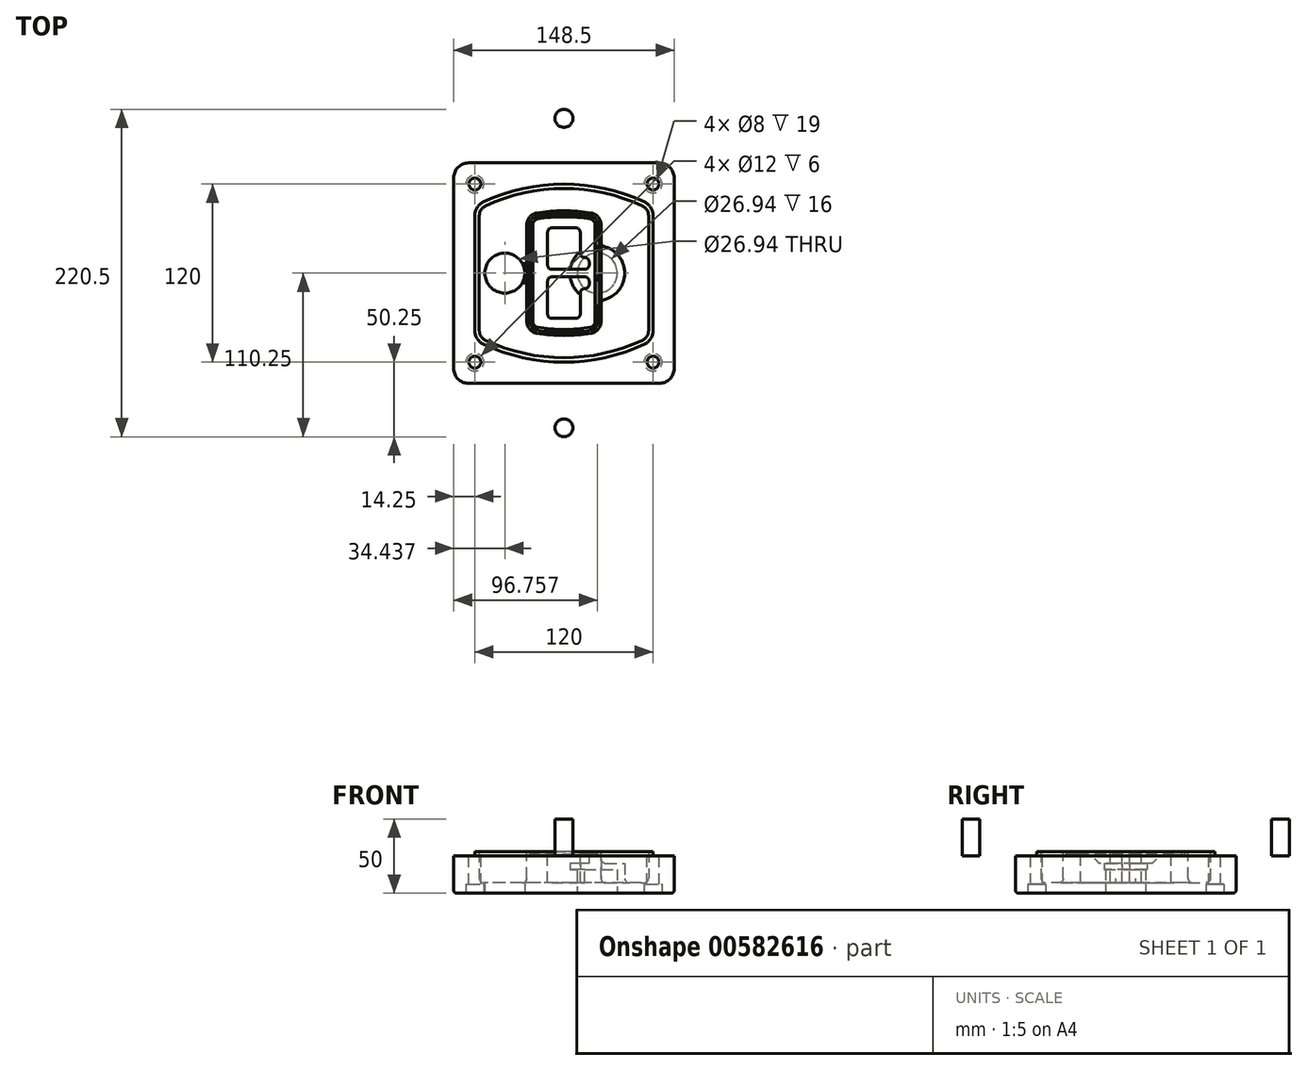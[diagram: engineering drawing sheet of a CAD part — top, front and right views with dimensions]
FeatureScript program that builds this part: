
annotation { "Feature Type Name" : "Feature", "Feature Type Description" : "" }
export const myFeature = defineFeature(function(context is Context, id is Id, definition is map)
    precondition{}
    {
        {
            var Q0;
            Q0=qCreatedBy(makeId("Top.planeOp"),FACE);
            var sketch = newSketch(context, id + "F0", { "sketchPlane" : qUnion([Q0])});
            skPoint(sketch, "E0.rect.middle", {"position": v(0, 0) * mm});
            skLineSegment(sketch, "E1.bottom", {"start": v(-64.25, -74.25) * mm, "end": v(64.25, -74.25) * mm});
            skLineSegment(sketch, "E1.top", {"start": v(-64.25, 74.25) * mm, "end": v(64.25, 74.25) * mm});
            skLineSegment(sketch, "E1.left", {"start": v(-74.25, -64.25) * mm, "end": v(-74.25, 64.25) * mm});
            skLineSegment(sketch, "E1.right", {"start": v(74.25, -64.25) * mm, "end": v(74.25, 64.25) * mm});
            skLineSegment(sketch, "E2", {"start": v(-74.25, 74.25) * mm, "end": v(74.25, -74.25) * mm, "construction": true});
            skLineSegment(sketch, "E3", {"start": v(74.25, 74.25) * mm, "end": v(-74.25, -74.25) * mm, "construction": true});
            skCircle(sketch, "E4", {"center": v(-60, 60) * mm, "radius": 4 * mm});
            skCircle(sketch, "E5", {"center": v(60, 60) * mm, "radius": 4 * mm});
            skCircle(sketch, "E6", {"center": v(60, -60) * mm, "radius": 4 * mm});
            skCircle(sketch, "E7", {"center": v(-60, -60) * mm, "radius": 4 * mm});
            skLineSegment(sketch, "E8", {"start": v(-60, 60) * mm, "end": v(60, 60) * mm, "construction": true});
            skLineSegment(sketch, "E9", {"start": v(60, 60) * mm, "end": v(60, -60) * mm, "construction": true});
            skLineSegment(sketch, "E10", {"start": v(60, -60) * mm, "end": v(-60, -60) * mm, "construction": true});
            skLineSegment(sketch, "E11", {"start": v(-60, -60) * mm, "end": v(-60, 60) * mm, "construction": true});
            skLineSegment(sketch, "E12", {"start": v(-60, 38.83) * mm, "end": v(-60, -38.83) * mm});
            skLineSegment(sketch, "E13", {"start": v(60, 38.83) * mm, "end": v(60, -38.83) * mm});
            skArc(sketch, "E14", {"start": v(54.26, 47.88) * mm, "mid": v(0, 60) * mm, "end": v(-54.26, 47.88) * mm});
            skArc(sketch, "E15", {"start": v(-54.26, -47.88) * mm, "mid": v(0, -60) * mm, "end": v(54.26, -47.88) * mm});
            skLineSegment(sketch, "E16", {"start": v(-60, 0) * mm, "end": v(60, 0) * mm, "construction": true});
            skPoint(sketch, "E17.visualSharp", {"position": v(-60, -45) * mm});
            skArc(sketch, "E17.filletArc", {"start": v(-60, -38.83) * mm, "mid": v(-58.44, -44.2) * mm, "end": v(-54.26, -47.88) * mm});
            skPoint(sketch, "E18.visualSharp", {"position": v(-60, 45) * mm});
            skArc(sketch, "E18.filletArc", {"start": v(-54.26, 47.88) * mm, "mid": v(-58.44, 44.2) * mm, "end": v(-60, 38.83) * mm});
            skPoint(sketch, "E19.visualSharp", {"position": v(60, 45) * mm});
            skArc(sketch, "E19.filletArc", {"start": v(60, 38.83) * mm, "mid": v(58.44, 44.2) * mm, "end": v(54.26, 47.88) * mm});
            skPoint(sketch, "E20.visualSharp", {"position": v(60, -45) * mm});
            skArc(sketch, "E20.filletArc", {"start": v(54.26, -47.88) * mm, "mid": v(58.44, -44.2) * mm, "end": v(60, -38.83) * mm});
            skPoint(sketch, "E21.visualSharp", {"position": v(-74.25, 74.25) * mm});
            skArc(sketch, "E21.filletArc", {"start": v(-64.25, 74.25) * mm, "mid": v(-71.32, 71.32) * mm, "end": v(-74.25, 64.25) * mm});
            skPoint(sketch, "E22.visualSharp", {"position": v(74.25, 74.25) * mm});
            skArc(sketch, "E22.filletArc", {"start": v(74.25, 64.25) * mm, "mid": v(71.32, 71.32) * mm, "end": v(64.25, 74.25) * mm});
            skPoint(sketch, "E23.visualSharp", {"position": v(74.25, -74.25) * mm});
            skArc(sketch, "E23.filletArc", {"start": v(64.25, -74.25) * mm, "mid": v(71.32, -71.32) * mm, "end": v(74.25, -64.25) * mm});
            skPoint(sketch, "E24.visualSharp", {"position": v(-74.25, -74.25) * mm});
            skArc(sketch, "E24.filletArc", {"start": v(-74.25, -64.25) * mm, "mid": v(-71.32, -71.32) * mm, "end": v(-64.25, -74.25) * mm});
            skArc(sketch, "E25.0", {"start": v(57, 38.83) * mm, "mid": v(55.9, 42.58) * mm, "end": v(52.98, 45.17) * mm});
            skLineSegment(sketch, "E25.1", {"start": v(57, 38.83) * mm, "end": v(57, -38.83) * mm});
            skArc(sketch, "E25.2", {"start": v(52.98, -45.17) * mm, "mid": v(55.9, -42.58) * mm, "end": v(57, -38.83) * mm});
            skArc(sketch, "E25.3", {"start": v(-52.98, -45.17) * mm, "mid": v(0, -57) * mm, "end": v(52.98, -45.17) * mm});
            skArc(sketch, "E25.4", {"start": v(-57, -38.83) * mm, "mid": v(-55.9, -42.58) * mm, "end": v(-52.98, -45.17) * mm});
            skArc(sketch, "E25.5", {"start": v(52.98, 45.17) * mm, "mid": v(0, 57) * mm, "end": v(-52.98, 45.17) * mm});
            skLineSegment(sketch, "E25.6", {"start": v(-57, 38.83) * mm, "end": v(-57, -38.83) * mm});
            skArc(sketch, "E25.7", {"start": v(-52.98, 45.17) * mm, "mid": v(-55.9, 42.58) * mm, "end": v(-57, 38.83) * mm});
            skArc(sketch, "E26.0", {"start": v(-55.96, 51.5) * mm, "mid": v(-61.82, 46.33) * mm, "end": v(-64, 38.83) * mm});
            skArc(sketch, "E26.1", {"start": v(55.96, 51.5) * mm, "mid": v(0, 64) * mm, "end": v(-55.96, 51.5) * mm});
            skArc(sketch, "E26.2", {"start": v(64, 38.83) * mm, "mid": v(61.82, 46.33) * mm, "end": v(55.96, 51.5) * mm});
            skLineSegment(sketch, "E26.3", {"start": v(64, 38.83) * mm, "end": v(64, -38.83) * mm});
            skArc(sketch, "E26.4", {"start": v(55.96, -51.5) * mm, "mid": v(61.82, -46.33) * mm, "end": v(64, -38.83) * mm});
            skLineSegment(sketch, "E26.5", {"start": v(-64, 38.83) * mm, "end": v(-64, -38.83) * mm});
            skArc(sketch, "E26.6", {"start": v(-55.96, -51.5) * mm, "mid": v(0, -64) * mm, "end": v(55.96, -51.5) * mm});
            skArc(sketch, "E26.7", {"start": v(-64, -38.83) * mm, "mid": v(-61.82, -46.33) * mm, "end": v(-55.96, -51.5) * mm});
            skSolve(sketch);
        }
        {
            var Q0;
            Q0=makeQuery(id+"F0.imprint","IMPRINT",FACE,{"disambiguationData":[TD([[makeQuery(id+"F0.imprint","IMPRINT",EDGE,{"derivedFrom":sQuery(id+"F0.wireOp",EDGE,"E1.bottom")}),1.0]])]});
            var Q1;
            Q1=makeQuery(id+"F0.imprint","IMPRINT",FACE,{"disambiguationData":[TD([[makeQuery(id+"F0.imprint","IMPRINT",EDGE,{"derivedFrom":sQuery(id+"F0.wireOp",EDGE,"E12")}),1.0]])]});
            var Q2;
            Q2=makeQuery(id+"F0.imprint","IMPRINT",FACE,{"disambiguationData":[TD([[makeQuery(id+"F0.imprint","IMPRINT",EDGE,{"derivedFrom":sQuery(id+"F0.wireOp",EDGE,"E25.0")}),1.0]])]});
            var Q3;
            Q3=makeQuery(id+"F0.imprint","IMPRINT",FACE,{"disambiguationData":[TD([[makeQuery(id+"F0.imprint","IMPRINT",EDGE,{"derivedFrom":sQuery(id+"F0.wireOp",EDGE,"E12")}),-1.0]])]});
            extrude(context, id + "F1", {"entities" : qUnion([Q0, Q1, Q2, Q3]), "oppositeDirection" : true, "depth" : 25 * mm});
        }
        {
            var Q0;
            Q0=makeQuery(id+"F0.imprint","IMPRINT",FACE,{"disambiguationData":[TD([[makeQuery(id+"F0.imprint","IMPRINT",EDGE,{"derivedFrom":sQuery(id+"F0.wireOp",EDGE,"E12")}),1.0]])]});
            extrude(context, id + "F2", {"entities" : qUnion([Q0]), "operationType" : NewBodyOperationType.ADD, "depth" : 3 * mm});
        }
        {
            var Q0;
            Q0=makeQuery(id+"F0.imprint","IMPRINT",FACE,{"disambiguationData":[TD([[makeQuery(id+"F0.imprint","IMPRINT",EDGE,{"derivedFrom":sQuery(id+"F0.wireOp",EDGE,"E25.0")}),1.0]])]});
            extrude(context, id + "F3", {"entities" : qUnion([Q0]), "operationType" : NewBodyOperationType.REMOVE, "oppositeDirection" : true, "depth" : 18 * mm});
        }
        {
            var Q0;
            Q0=makeQuery(id+"F2.opExtrude","CAP_FACE",FACE,{"disambiguationData":[OSD([sQuery(id+"F0.wireOp",EDGE,"E12"),sQuery(id+"F0.wireOp",EDGE,"E13"),sQuery(id+"F0.wireOp",EDGE,"E14"),sQuery(id+"F0.wireOp",EDGE,"E15"),sQuery(id+"F0.wireOp",EDGE,"E17.filletArc"),sQuery(id+"F0.wireOp",EDGE,"E18.filletArc"),sQuery(id+"F0.wireOp",EDGE,"E19.filletArc"),sQuery(id+"F0.wireOp",EDGE,"E20.filletArc"),sQuery(id+"F0.wireOp",EDGE,"E25.0"),sQuery(id+"F0.wireOp",EDGE,"E25.1"),sQuery(id+"F0.wireOp",EDGE,"E25.2"),sQuery(id+"F0.wireOp",EDGE,"E25.3"),sQuery(id+"F0.wireOp",EDGE,"E25.4"),sQuery(id+"F0.wireOp",EDGE,"E25.5"),sQuery(id+"F0.wireOp",EDGE,"E25.6"),sQuery(id+"F0.wireOp",EDGE,"E25.7")])],"isStart":false});
            var sketch = newSketch(context, id + "F4", { "sketchPlane" : qUnion([Q0])});
            skArc(sketch, "E27.0", {"start": v(-18.34, -40.45) * mm, "mid": v(0, -42) * mm, "end": v(18.34, -40.45) * mm});
            skArc(sketch, "E28.0", {"start": v(18.34, 40.45) * mm, "mid": v(0, 42) * mm, "end": v(-18.34, 40.45) * mm});
            skLineSegment(sketch, "E29", {"start": v(-25, 32.57) * mm, "end": v(-25, -32.57) * mm});
            skLineSegment(sketch, "E30", {"start": v(25, 32.57) * mm, "end": v(25, -32.57) * mm});
            skLineSegment(sketch, "E31", {"start": v(-25, 39.1) * mm, "end": v(25, 39.1) * mm, "construction": true});
            skLineSegment(sketch, "E32", {"start": v(-25, -39.1) * mm, "end": v(25, -39.1) * mm, "construction": true});
            skPoint(sketch, "E33.visualSharp", {"position": v(-25, 39.1) * mm});
            skArc(sketch, "E33.filletArc", {"start": v(-18.34, 40.45) * mm, "mid": v(-23.11, 37.73) * mm, "end": v(-25, 32.57) * mm});
            skPoint(sketch, "E34.visualSharp", {"position": v(25, 39.1) * mm});
            skArc(sketch, "E34.filletArc", {"start": v(25, 32.57) * mm, "mid": v(23.11, 37.73) * mm, "end": v(18.34, 40.45) * mm});
            skPoint(sketch, "E35.visualSharp", {"position": v(25, -39.1) * mm});
            skArc(sketch, "E35.filletArc", {"start": v(18.34, -40.45) * mm, "mid": v(23.11, -37.73) * mm, "end": v(25, -32.57) * mm});
            skPoint(sketch, "E36.visualSharp", {"position": v(-25, -39.1) * mm});
            skArc(sketch, "E36.filletArc", {"start": v(-25, -32.57) * mm, "mid": v(-23.11, -37.73) * mm, "end": v(-18.34, -40.45) * mm});
            skArc(sketch, "E37.0", {"start": v(52.98, 45.17) * mm, "mid": v(0, 57) * mm, "end": v(-52.98, 45.17) * mm});
            skArc(sketch, "E37.1", {"start": v(-52.98, 45.17) * mm, "mid": v(-55.9, 42.58) * mm, "end": v(-57, 38.83) * mm});
            skLineSegment(sketch, "E37.2", {"start": v(-57, 38.83) * mm, "end": v(-57, -38.83) * mm});
            skArc(sketch, "E37.3", {"start": v(-57, -38.83) * mm, "mid": v(-55.9, -42.58) * mm, "end": v(-52.98, -45.17) * mm});
            skArc(sketch, "E37.4", {"start": v(-52.98, -45.17) * mm, "mid": v(0, -57) * mm, "end": v(52.98, -45.17) * mm});
            skArc(sketch, "E37.5", {"start": v(52.98, -45.17) * mm, "mid": v(55.9, -42.58) * mm, "end": v(57, -38.83) * mm});
            skLineSegment(sketch, "E37.6", {"start": v(57, 38.83) * mm, "end": v(57, -38.83) * mm});
            skArc(sketch, "E37.7", {"start": v(57, 38.83) * mm, "mid": v(55.9, 42.58) * mm, "end": v(52.98, 45.17) * mm});
            skLineSegment(sketch, "E38.0", {"start": v(23, 32.57) * mm, "end": v(23, -32.57) * mm});
            skArc(sketch, "E38.1", {"start": v(18, -38.48) * mm, "mid": v(21.58, -36.44) * mm, "end": v(23, -32.57) * mm});
            skArc(sketch, "E38.2", {"start": v(-18, -38.48) * mm, "mid": v(0, -40) * mm, "end": v(18, -38.48) * mm});
            skArc(sketch, "E38.3", {"start": v(-23, -32.57) * mm, "mid": v(-21.58, -36.44) * mm, "end": v(-18, -38.48) * mm});
            skLineSegment(sketch, "E38.4", {"start": v(-23, 32.57) * mm, "end": v(-23, -32.57) * mm});
            skArc(sketch, "E38.5", {"start": v(23, 32.57) * mm, "mid": v(21.58, 36.44) * mm, "end": v(18, 38.48) * mm});
            skArc(sketch, "E38.6", {"start": v(-18, 38.48) * mm, "mid": v(-21.58, 36.44) * mm, "end": v(-23, 32.57) * mm});
            skArc(sketch, "E38.7", {"start": v(18, 38.48) * mm, "mid": v(0, 40) * mm, "end": v(-18, 38.48) * mm});
            skArc(sketch, "E39.0", {"start": v(21, 32.57) * mm, "mid": v(20.06, 35.15) * mm, "end": v(17.67, 36.5) * mm});
            skLineSegment(sketch, "E39.1", {"start": v(21, 32.57) * mm, "end": v(21, -32.57) * mm});
            skArc(sketch, "E39.2", {"start": v(17.67, -36.5) * mm, "mid": v(20.06, -35.15) * mm, "end": v(21, -32.57) * mm});
            skArc(sketch, "E39.3", {"start": v(-17.67, -36.5) * mm, "mid": v(0, -38) * mm, "end": v(17.67, -36.5) * mm});
            skArc(sketch, "E39.4", {"start": v(-21, -32.57) * mm, "mid": v(-20.06, -35.15) * mm, "end": v(-17.67, -36.5) * mm});
            skArc(sketch, "E39.5", {"start": v(17.67, 36.5) * mm, "mid": v(0, 38) * mm, "end": v(-17.67, 36.5) * mm});
            skLineSegment(sketch, "E39.6", {"start": v(-21, 32.57) * mm, "end": v(-21, -32.57) * mm});
            skArc(sketch, "E39.7", {"start": v(-17.67, 36.5) * mm, "mid": v(-20.06, 35.15) * mm, "end": v(-21, 32.57) * mm});
            skLineSegment(sketch, "E40", {"start": v(-25, 0) * mm, "end": v(25, 0) * mm, "construction": true});
            skLineSegment(sketch, "E41", {"start": v(-11, 5.5) * mm, "end": v(-11, 27.5) * mm});
            skLineSegment(sketch, "E42", {"start": v(-8, 30.5) * mm, "end": v(8, 30.5) * mm});
            skLineSegment(sketch, "E43", {"start": v(11, 27.5) * mm, "end": v(11, 13.5) * mm});
            skLineSegment(sketch, "E44", {"start": v(14, 10.5) * mm, "end": v(14, 10.5) * mm});
            skLineSegment(sketch, "E45", {"start": v(17, 7.5) * mm, "end": v(17, 5.5) * mm});
            skLineSegment(sketch, "E46", {"start": v(14, 2.5) * mm, "end": v(-8, 2.5) * mm});
            skPoint(sketch, "E47.visualSharp", {"position": v(-11, 30.5) * mm});
            skArc(sketch, "E47.filletArc", {"start": v(-8, 30.5) * mm, "mid": v(-10.12, 29.62) * mm, "end": v(-11, 27.5) * mm});
            skPoint(sketch, "E48.visualSharp", {"position": v(11, 30.5) * mm});
            skArc(sketch, "E48.filletArc", {"start": v(11, 27.5) * mm, "mid": v(10.12, 29.62) * mm, "end": v(8, 30.5) * mm});
            skPoint(sketch, "E49.visualSharp", {"position": v(11, 10.5) * mm});
            skArc(sketch, "E49.filletArc", {"start": v(11, 13.5) * mm, "mid": v(11.88, 11.38) * mm, "end": v(14, 10.5) * mm});
            skPoint(sketch, "E50.visualSharp", {"position": v(17, 10.5) * mm});
            skArc(sketch, "E50.filletArc", {"start": v(17, 7.5) * mm, "mid": v(16.12, 9.62) * mm, "end": v(14, 10.5) * mm});
            skPoint(sketch, "E51.visualSharp", {"position": v(17, 2.5) * mm});
            skArc(sketch, "E51.filletArc", {"start": v(14, 2.5) * mm, "mid": v(16.12, 3.38) * mm, "end": v(17, 5.5) * mm});
            skPoint(sketch, "E52.visualSharp", {"position": v(-11, 2.5) * mm});
            skArc(sketch, "E52.filletArc", {"start": v(-11, 5.5) * mm, "mid": v(-10.12, 3.38) * mm, "end": v(-8, 2.5) * mm});
            skLineSegment(sketch, "E53.0.MirrorCS", {"start": v(14, -2.5) * mm, "end": v(-8, -2.5) * mm});
            skArc(sketch, "E54.0.MirrorCS", {"start": v(-11, -5.5) * mm, "mid": v(-10.12, -3.38) * mm, "end": v(-8, -2.5) * mm});
            skLineSegment(sketch, "E55.0.MirrorCS", {"start": v(-11, -5.5) * mm, "end": v(-11, -27.5) * mm});
            skArc(sketch, "E56.0.MirrorCS", {"start": v(-8, -30.5) * mm, "mid": v(-10.12, -29.62) * mm, "end": v(-11, -27.5) * mm});
            skLineSegment(sketch, "E57.0.MirrorCS", {"start": v(-8, -30.5) * mm, "end": v(8, -30.5) * mm});
            skArc(sketch, "E58.0.MirrorCS", {"start": v(11, -27.5) * mm, "mid": v(10.12, -29.62) * mm, "end": v(8, -30.5) * mm});
            skLineSegment(sketch, "E59.0.MirrorCS", {"start": v(11, -27.5) * mm, "end": v(11, -13.5) * mm});
            skArc(sketch, "E60.0.MirrorCS", {"start": v(11, -13.5) * mm, "mid": v(11.88, -11.38) * mm, "end": v(14, -10.5) * mm});
            skArc(sketch, "E61.0.MirrorCS", {"start": v(17, -7.5) * mm, "mid": v(16.12, -9.62) * mm, "end": v(14, -10.5) * mm});
            skLineSegment(sketch, "E62.0.MirrorCS", {"start": v(17, -7.5) * mm, "end": v(17, -5.5) * mm});
            skArc(sketch, "E63.0.MirrorCS", {"start": v(14, -2.5) * mm, "mid": v(16.12, -3.38) * mm, "end": v(17, -5.5) * mm});
            skSolve(sketch);
        }
        {
            var Q0;
            Q0=makeQuery(id+"F4.imprint","IMPRINT",FACE,{"disambiguationData":[TD([[makeQuery(id+"F4.imprint","IMPRINT",EDGE,{"derivedFrom":sQuery(id+"F4.wireOp",EDGE,"E27.0")}),1.0]])]});
            var Q1;
            Q1=makeQuery(id+"F4.imprint","IMPRINT",FACE,{"disambiguationData":[TD([[makeQuery(id+"F4.imprint","IMPRINT",EDGE,{"derivedFrom":sQuery(id+"F4.wireOp",EDGE,"E38.0")}),-1.0]])]});
            var Q2;
            Q2=makeQuery(id+"F4.imprint","IMPRINT",FACE,{"disambiguationData":[TD([[makeQuery(id+"F4.imprint","IMPRINT",EDGE,{"derivedFrom":sQuery(id+"F4.wireOp",EDGE,"E39.0")}),1.0]])]});
            extrude(context, id + "F5", {"entities" : qUnion([Q0, Q1, Q2]), "operationType" : NewBodyOperationType.ADD, "endBound" : BoundingType.UP_TO_NEXT, "oppositeDirection" : true, "depth" : 25 * mm});
        }
        {
            var Q0;
            Q0=makeQuery(id+"F4.imprint","IMPRINT",FACE,{"disambiguationData":[TD([[makeQuery(id+"F4.imprint","IMPRINT",EDGE,{"derivedFrom":sQuery(id+"F4.wireOp",EDGE,"E38.0")}),-1.0]])]});
            extrude(context, id + "F6", {"entities" : qUnion([Q0]), "operationType" : NewBodyOperationType.REMOVE, "oppositeDirection" : true, "depth" : 2 * mm});
        }
        {
            var Q0;
            Q0=makeQuery(id+"F1.opExtrude","CAP_FACE",FACE,{"disambiguationData":[OSD([sQuery(id+"F0.wireOp",EDGE,"E1.bottom"),sQuery(id+"F0.wireOp",EDGE,"E1.top"),sQuery(id+"F0.wireOp",EDGE,"E1.left"),sQuery(id+"F0.wireOp",EDGE,"E1.right"),sQuery(id+"F0.wireOp",EDGE,"E4"),sQuery(id+"F0.wireOp",EDGE,"E5"),sQuery(id+"F0.wireOp",EDGE,"E6"),sQuery(id+"F0.wireOp",EDGE,"E7"),sQuery(id+"F0.wireOp",EDGE,"E21.filletArc"),sQuery(id+"F0.wireOp",EDGE,"E22.filletArc"),sQuery(id+"F0.wireOp",EDGE,"E23.filletArc"),sQuery(id+"F0.wireOp",EDGE,"E24.filletArc")])],"isStart":false});
            var sketch = newSketch(context, id + "F7", { "sketchPlane" : qUnion([Q0])});
            skCircle(sketch, "E64", {"center": v(22.5, 0) * mm, "radius": 13.47 * mm});
            skCircle(sketch, "E65", {"center": v(-39.81, 0) * mm, "radius": 13.47 * mm});
            skLineSegment(sketch, "E66", {"start": v(74.25, 0) * mm, "end": v(-74.25, 0) * mm});
            skCircle(sketch, "E67", {"center": v(22.5, 0) * mm, "radius": 18.47 * mm});
            skCircle(sketch, "E68", {"center": v(60, -60) * mm, "radius": 6 * mm});
            skCircle(sketch, "E69", {"center": v(-60, -60) * mm, "radius": 6 * mm});
            skCircle(sketch, "E70", {"center": v(-60, 60) * mm, "radius": 6 * mm});
            skCircle(sketch, "E71", {"center": v(60, 60) * mm, "radius": 6 * mm});
            skSolve(sketch);
        }
        {
            var Q0;
            {var subQ1=sQuery(id+"F7.wireOp",EDGE,"E66");var subQ4=sQuery(id+"F7.wireOp",EDGE,"E64");var subQ6=makeQuery(id+"F7.imprint","INTERSECT",VERTEX,{"disambiguationData":[OD(0.0)],"derivedFrom":[subQ4,subQ1]});Q0=makeQuery(id+"F7.imprint","IMPRINT",FACE,{"disambiguationData":[TD([[makeQuery(id+"F7.imprint","IMPRINT",EDGE,{"disambiguationData":[TD([[subQ6,-1.0]])],"derivedFrom":subQ4}),-1.0]])]});}
            var Q1;
            {var subQ0=sQuery(id+"F7.wireOp",EDGE,"E66");var subQ1=sQuery(id+"F7.wireOp",EDGE,"E64");var subQ3=makeQuery(id+"F7.imprint","INTERSECT",VERTEX,{"disambiguationData":[OD(0.0)],"derivedFrom":[subQ1,subQ0]});Q1=makeQuery(id+"F7.imprint","IMPRINT",FACE,{"disambiguationData":[TD([[makeQuery(id+"F7.imprint","IMPRINT",EDGE,{"disambiguationData":[TD([[subQ3,-1.0]])],"derivedFrom":subQ1}),1.0]])]});}
            var Q2;
            {var subQ0=sQuery(id+"F7.wireOp",EDGE,"E66");var subQ1=sQuery(id+"F7.wireOp",EDGE,"E64");var subQ3=makeQuery(id+"F7.imprint","INTERSECT",VERTEX,{"disambiguationData":[OD(0.0)],"derivedFrom":[subQ1,subQ0]});Q2=makeQuery(id+"F7.imprint","IMPRINT",FACE,{"disambiguationData":[TD([[makeQuery(id+"F7.imprint","IMPRINT",EDGE,{"disambiguationData":[TD([[subQ3,1.0]])],"derivedFrom":subQ1}),1.0]])]});}
            var Q3;
            {var subQ1=sQuery(id+"F7.wireOp",EDGE,"E66");var subQ4=sQuery(id+"F7.wireOp",EDGE,"E64");var subQ6=makeQuery(id+"F7.imprint","INTERSECT",VERTEX,{"disambiguationData":[OD(0.0)],"derivedFrom":[subQ4,subQ1]});Q3=makeQuery(id+"F7.imprint","IMPRINT",FACE,{"disambiguationData":[TD([[makeQuery(id+"F7.imprint","IMPRINT",EDGE,{"disambiguationData":[TD([[subQ6,1.0]])],"derivedFrom":subQ4}),-1.0]])]});}
            extrude(context, id + "F8", {"entities" : qUnion([Q0, Q1, Q2, Q3]), "operationType" : NewBodyOperationType.ADD, "oppositeDirection" : true, "depth" : 20 * mm});
        }
        {
            var Q0;
            {var subQ0=sQuery(id+"F7.wireOp",EDGE,"E66");var subQ1=sQuery(id+"F7.wireOp",EDGE,"E64");var subQ3=makeQuery(id+"F7.imprint","INTERSECT",VERTEX,{"disambiguationData":[OD(0.0)],"derivedFrom":[subQ1,subQ0]});Q0=makeQuery(id+"F7.imprint","IMPRINT",FACE,{"disambiguationData":[TD([[makeQuery(id+"F7.imprint","IMPRINT",EDGE,{"disambiguationData":[TD([[subQ3,-1.0]])],"derivedFrom":subQ1}),1.0]])]});}
            var Q1;
            {var subQ0=sQuery(id+"F7.wireOp",EDGE,"E66");var subQ1=sQuery(id+"F7.wireOp",EDGE,"E64");var subQ3=makeQuery(id+"F7.imprint","INTERSECT",VERTEX,{"disambiguationData":[OD(0.0)],"derivedFrom":[subQ1,subQ0]});Q1=makeQuery(id+"F7.imprint","IMPRINT",FACE,{"disambiguationData":[TD([[makeQuery(id+"F7.imprint","IMPRINT",EDGE,{"disambiguationData":[TD([[subQ3,1.0]])],"derivedFrom":subQ1}),1.0]])]});}
            extrude(context, id + "F9", {"entities" : qUnion([Q0, Q1]), "operationType" : NewBodyOperationType.REMOVE, "oppositeDirection" : true, "depth" : 16 * mm});
        }
        {
            var Q0;
            {var subQ0=sQuery(id+"F7.wireOp",EDGE,"E66");var subQ1=sQuery(id+"F7.wireOp",EDGE,"E65");var subQ3=makeQuery(id+"F7.imprint","INTERSECT",VERTEX,{"disambiguationData":[OD(0.0)],"derivedFrom":[subQ1,subQ0]});Q0=makeQuery(id+"F7.imprint","IMPRINT",FACE,{"disambiguationData":[TD([[makeQuery(id+"F7.imprint","IMPRINT",EDGE,{"disambiguationData":[TD([[subQ3,-1.0]])],"derivedFrom":subQ1}),1.0]])]});}
            var Q1;
            {var subQ0=sQuery(id+"F7.wireOp",EDGE,"E66");var subQ1=sQuery(id+"F7.wireOp",EDGE,"E65");var subQ3=makeQuery(id+"F7.imprint","INTERSECT",VERTEX,{"disambiguationData":[OD(0.0)],"derivedFrom":[subQ1,subQ0]});Q1=makeQuery(id+"F7.imprint","IMPRINT",FACE,{"disambiguationData":[TD([[makeQuery(id+"F7.imprint","IMPRINT",EDGE,{"disambiguationData":[TD([[subQ3,1.0]])],"derivedFrom":subQ1}),1.0]])]});}
            extrude(context, id + "F10", {"entities" : qUnion([Q0, Q1]), "operationType" : NewBodyOperationType.REMOVE, "oppositeDirection" : true, "depth" : 25 * mm});
        }
        {
            var Q0;
            Q0=makeQuery(id+"F7.imprint","IMPRINT",FACE,{"disambiguationData":[TD([[makeQuery(id+"F7.imprint","IMPRINT",EDGE,{"derivedFrom":sQuery(id+"F7.wireOp",EDGE,"E68")}),1.0]])]});
            var Q1;
            Q1=makeQuery(id+"F7.imprint","IMPRINT",FACE,{"disambiguationData":[TD([[makeQuery(id+"F7.imprint","IMPRINT",EDGE,{"derivedFrom":makeQuery(id+"F1.opExtrude","CAP_EDGE",EDGE,{"disambiguationData":[OSD([sQuery(id+"F0.wireOp",EDGE,"E5")])],"isStart":false})}),-1.0]])]});
            var Q2;
            Q2=makeQuery(id+"F7.imprint","IMPRINT",FACE,{"disambiguationData":[TD([[makeQuery(id+"F7.imprint","IMPRINT",EDGE,{"derivedFrom":sQuery(id+"F7.wireOp",EDGE,"E69")}),1.0]])]});
            var Q3;
            Q3=makeQuery(id+"F7.imprint","IMPRINT",FACE,{"disambiguationData":[TD([[makeQuery(id+"F7.imprint","IMPRINT",EDGE,{"derivedFrom":makeQuery(id+"F1.opExtrude","CAP_EDGE",EDGE,{"disambiguationData":[OSD([sQuery(id+"F0.wireOp",EDGE,"E4")])],"isStart":false})}),-1.0]])]});
            var Q4;
            Q4=makeQuery(id+"F7.imprint","IMPRINT",FACE,{"disambiguationData":[TD([[makeQuery(id+"F7.imprint","IMPRINT",EDGE,{"derivedFrom":sQuery(id+"F7.wireOp",EDGE,"E70")}),1.0]])]});
            var Q5;
            Q5=makeQuery(id+"F7.imprint","IMPRINT",FACE,{"disambiguationData":[TD([[makeQuery(id+"F7.imprint","IMPRINT",EDGE,{"derivedFrom":makeQuery(id+"F1.opExtrude","CAP_EDGE",EDGE,{"disambiguationData":[OSD([sQuery(id+"F0.wireOp",EDGE,"E7")])],"isStart":false})}),-1.0]])]});
            var Q6;
            Q6=makeQuery(id+"F7.imprint","IMPRINT",FACE,{"disambiguationData":[TD([[makeQuery(id+"F7.imprint","IMPRINT",EDGE,{"derivedFrom":sQuery(id+"F7.wireOp",EDGE,"E71")}),1.0]])]});
            var Q7;
            Q7=makeQuery(id+"F7.imprint","IMPRINT",FACE,{"disambiguationData":[TD([[makeQuery(id+"F7.imprint","IMPRINT",EDGE,{"derivedFrom":makeQuery(id+"F1.opExtrude","CAP_EDGE",EDGE,{"disambiguationData":[OSD([sQuery(id+"F0.wireOp",EDGE,"E6")])],"isStart":false})}),-1.0]])]});
            extrude(context, id + "F11", {"entities" : qUnion([Q0, Q1, Q2, Q3, Q4, Q5, Q6, Q7]), "operationType" : NewBodyOperationType.REMOVE, "oppositeDirection" : true, "depth" : 6 * mm});
        }
        {
            var Q0;
            Q0=makeQuery(id+"F9.boolean.opBoolean","COPY",FACE,{"derivedFrom":makeQuery(id+"F9.opExtrude","CAP_FACE",FACE,{"disambiguationData":[OSD([sQuery(id+"F7.wireOp",EDGE,"E64")])],"isStart":false})});
            var sketch = newSketch(context, id + "F12", { "sketchPlane" : qUnion([Q0])});
            skArc(sketch, "E72.0", {"start": v(11, 14.45) * mm, "mid": v(6.45, 9.13) * mm, "end": v(4.2, 2.5) * mm});
            skArc(sketch, "E72.1", {"start": v(4.2, -2.5) * mm, "mid": v(6.45, -9.13) * mm, "end": v(11, -14.45) * mm});
            skLineSegment(sketch, "E73", {"start": v(4.2, -2.5) * mm, "end": v(14, -2.5) * mm});
            skLineSegment(sketch, "E74.0", {"start": v(14, 2.5) * mm, "end": v(4.2, 2.5) * mm});
            skArc(sketch, "E74.1", {"start": v(14, 2.5) * mm, "mid": v(16.12, 3.38) * mm, "end": v(17, 5.5) * mm});
            skLineSegment(sketch, "E74.2", {"start": v(17, 7.5) * mm, "end": v(17, 5.5) * mm});
            skArc(sketch, "E74.3", {"start": v(17, 7.5) * mm, "mid": v(16.12, 9.62) * mm, "end": v(14, 10.5) * mm});
            skArc(sketch, "E74.4", {"start": v(11, 13.5) * mm, "mid": v(11.88, 11.38) * mm, "end": v(14, 10.5) * mm});
            skLineSegment(sketch, "E74.5", {"start": v(11, 14.45) * mm, "end": v(11, 13.5) * mm});
            skLineSegment(sketch, "E74.7", {"start": v(14, -2.5) * mm, "end": v(4.2, -2.5) * mm});
            skArc(sketch, "E74.8", {"start": v(14, -2.5) * mm, "mid": v(16.12, -3.38) * mm, "end": v(17, -5.5) * mm});
            skLineSegment(sketch, "E74.9", {"start": v(17, -7.5) * mm, "end": v(17, -5.5) * mm});
            skArc(sketch, "E74.10", {"start": v(17, -7.5) * mm, "mid": v(16.12, -9.62) * mm, "end": v(14, -10.5) * mm});
            skArc(sketch, "E74.11", {"start": v(11, -13.5) * mm, "mid": v(11.88, -11.38) * mm, "end": v(14, -10.5) * mm});
            skLineSegment(sketch, "E74.12", {"start": v(11, -14.45) * mm, "end": v(11, -13.5) * mm});
            skPoint(sketch, "E75.orphan", {"position": v(11, -27.5) * mm});
            skPoint(sketch, "E76.orphan", {"position": v(-8, -2.5) * mm});
            skPoint(sketch, "E77.orphan", {"position": v(-8, 2.5) * mm});
            skPoint(sketch, "E78.orphan", {"position": v(11, 27.5) * mm});
            skSolve(sketch);
        }
        {
            var Q0;
            {var subQ7=sQuery(id+"F12.wireOp",EDGE,"E72.0");var subQ14=sQuery(id+"F12.wireOp",EDGE,"E72.1");var subQ16=sQuery(id+"F12.wireOp",EDGE,"E74.1");var subQ18=sQuery(id+"F12.wireOp",EDGE,"E74.8");Q0=qUnion([makeQuery(id+"F12.imprint","IMPRINT",FACE,{"disambiguationData":[TD([[makeQuery(id+"F12.imprint","IMPRINT",EDGE,{"derivedFrom":subQ7}),1.0]])]}),makeQuery(id+"F12.imprint","IMPRINT",FACE,{"disambiguationData":[TD([[makeQuery(id+"F12.imprint","IMPRINT",EDGE,{"derivedFrom":subQ14}),1.0]])]}),makeQuery(id+"F12.imprint","IMPRINT",FACE,{"disambiguationData":[TD([[makeQuery(id+"F12.imprint","IMPRINT",EDGE,{"derivedFrom":subQ16}),1.0]])]}),makeQuery(id+"F12.imprint","IMPRINT",FACE,{"disambiguationData":[TD([[makeQuery(id+"F12.imprint","IMPRINT",EDGE,{"derivedFrom":subQ18}),-1.0]])]})]);}
            var Q1;
            Q1=makeQuery(id+"F5.boolean.opBoolean","SPLIT",FACE,{"disambiguationData":[TD([makeQuery(id+"F5.opExtrude","SWEPT_FACE",FACE,{"disambiguationData":[OSD([sQuery(id+"F4.wireOp",EDGE,"E41")])]})])],"derivedFrom":makeQuery(id+"F3.boolean.opBoolean","COPY",FACE,{"derivedFrom":makeQuery(id+"F3.opExtrude","CAP_FACE",FACE,{"disambiguationData":[OSD([sQuery(id+"F0.wireOp",EDGE,"E25.0"),sQuery(id+"F0.wireOp",EDGE,"E25.1"),sQuery(id+"F0.wireOp",EDGE,"E25.2"),sQuery(id+"F0.wireOp",EDGE,"E25.3"),sQuery(id+"F0.wireOp",EDGE,"E25.4"),sQuery(id+"F0.wireOp",EDGE,"E25.5"),sQuery(id+"F0.wireOp",EDGE,"E25.6"),sQuery(id+"F0.wireOp",EDGE,"E25.7")])],"isStart":false})})});
            extrude(context, id + "F13", {"entities" : qUnion([Q0]), "operationType" : NewBodyOperationType.REMOVE, "endBound" : BoundingType.UP_TO_SURFACE, "endBoundEntityFace" : qUnion([Q1]), "depth" : 25 * mm});
        }
        {
            var Q0;
            Q0=makeQuery(id+"F3.boolean.opBoolean","COPY",EDGE,{"derivedFrom":makeQuery(id+"F3.opExtrude","CAP_EDGE",EDGE,{"disambiguationData":[OSD([sQuery(id+"F0.wireOp",EDGE,"E25.6")])],"isStart":false})});
            var Q1;
            Q1=makeQuery(id+"F8.boolean.opBoolean","INTERSECT",EDGE,{"derivedFrom":[makeQuery(id+"F5.opExtrude","SWEPT_FACE",FACE,{"disambiguationData":[OSD([sQuery(id+"F4.wireOp",EDGE,"E30")])]}),makeQuery(id+"F8.opExtrude","CAP_FACE",FACE,{"disambiguationData":[OSD([sQuery(id+"F7.wireOp",EDGE,"E67")])],"isStart":false})]});
            var Q2;
            Q2=makeQuery(id+"F8.boolean.opBoolean","INTERSECT",EDGE,{"disambiguationData":[OD(1.0)],"derivedFrom":[makeQuery(id+"F5.opExtrude","SWEPT_FACE",FACE,{"disambiguationData":[OSD([sQuery(id+"F4.wireOp",EDGE,"E30")])]}),makeQuery(id+"F8.opExtrude","SWEPT_FACE",FACE,{"disambiguationData":[OSD([sQuery(id+"F7.wireOp",EDGE,"E67")])]})]});
            var Q3;
            {var subQ0=sQuery(id+"F4.wireOp",EDGE,"E30");Q3=makeQuery(id+"F8.boolean.opBoolean","SPLIT",EDGE,{"disambiguationData":[TD([makeQuery(id+"F5.opExtrude","SWEPT_FACE",FACE,{"disambiguationData":[OSD([sQuery(id+"F4.wireOp",EDGE,"E35.filletArc")])]})])],"derivedFrom":makeQuery(id+"F5.opExtrude","CAP_EDGE",EDGE,{"disambiguationData":[OSD([subQ0])],"isStart":false})});}
            var Q4;
            {var subQ0=sQuery(id+"F0.wireOp",EDGE,"E25.7");var subQ1=sQuery(id+"F0.wireOp",EDGE,"E25.1");var subQ2=sQuery(id+"F0.wireOp",EDGE,"E25.6");var subQ3=sQuery(id+"F0.wireOp",EDGE,"E25.5");var subQ4=sQuery(id+"F0.wireOp",EDGE,"E25.4");var subQ5=sQuery(id+"F0.wireOp",EDGE,"E25.0");var subQ6=sQuery(id+"F0.wireOp",EDGE,"E25.2");var subQ7=sQuery(id+"F0.wireOp",EDGE,"E25.3");Q4=makeQuery(id+"F8.boolean.opBoolean","INTERSECT",EDGE,{"derivedFrom":[makeQuery(id+"F5.boolean.opBoolean","SPLIT",FACE,{"disambiguationData":[TD([makeQuery(id+"F2.opExtrude","SWEPT_FACE",FACE,{"disambiguationData":[OSD([subQ5])]})])],"derivedFrom":makeQuery(id+"F3.boolean.opBoolean","COPY",FACE,{"derivedFrom":makeQuery(id+"F3.opExtrude","CAP_FACE",FACE,{"disambiguationData":[OSD([subQ5,subQ1,subQ6,subQ7,subQ4,subQ3,subQ2,subQ0])],"isStart":false})})}),makeQuery(id+"F8.opExtrude","SWEPT_FACE",FACE,{"disambiguationData":[OSD([sQuery(id+"F7.wireOp",EDGE,"E67")])]})]});}
            var Q5;
            Q5=makeQuery(id+"F8.boolean.opBoolean","INTERSECT",EDGE,{"disambiguationData":[OD(0.0)],"derivedFrom":[makeQuery(id+"F5.opExtrude","SWEPT_FACE",FACE,{"disambiguationData":[OSD([sQuery(id+"F4.wireOp",EDGE,"E30")])]}),makeQuery(id+"F8.opExtrude","SWEPT_FACE",FACE,{"disambiguationData":[OSD([sQuery(id+"F7.wireOp",EDGE,"E67")])]})]});
            fillet(context, id + "F14", {"entities" : qUnion([Q0, Q1, Q2, Q3, Q4, Q5]), "radius" : 3 * mm, "tangentPropagation" : true, "allowEdgeOverflow" : false});
        }
        {
            var Q0;
            Q0=makeQuery(id+"F1.opExtrude","CAP_EDGE",EDGE,{"disambiguationData":[OSD([sQuery(id+"F0.wireOp",EDGE,"E1.bottom")])],"isStart":false});
            fillet(context, id + "F15", {"entities" : qUnion([Q0]), "radius" : 2 * mm, "tangentPropagation" : true, "allowEdgeOverflow" : false});
        }
        {
            var Q0;
            {var subQ0=sQuery(id+"F0.wireOp",EDGE,"E21.filletArc");var subQ1=sQuery(id+"F0.wireOp",EDGE,"E7");var subQ2=sQuery(id+"F0.wireOp",EDGE,"E6");var subQ3=sQuery(id+"F0.wireOp",EDGE,"E5");var subQ4=sQuery(id+"F0.wireOp",EDGE,"E4");var subQ5=sQuery(id+"F0.wireOp",EDGE,"E22.filletArc");var subQ6=sQuery(id+"F0.wireOp",EDGE,"E1.bottom");var subQ7=sQuery(id+"F0.wireOp",EDGE,"E1.right");var subQ8=sQuery(id+"F0.wireOp",EDGE,"E1.top");var subQ9=sQuery(id+"F0.wireOp",EDGE,"E1.left");var subQ10=sQuery(id+"F0.wireOp",EDGE,"E23.filletArc");var subQ11=sQuery(id+"F0.wireOp",EDGE,"E24.filletArc");Q0=makeQuery(id+"F2.boolean.opBoolean","SPLIT",FACE,{"disambiguationData":[TD([makeQuery(id+"F1.opExtrude","SWEPT_FACE",FACE,{"disambiguationData":[OSD([subQ6])]})])],"derivedFrom":makeQuery(id+"F1.opExtrude","CAP_FACE",FACE,{"disambiguationData":[OSD([subQ6,subQ8,subQ9,subQ7,subQ4,subQ3,subQ2,subQ1,subQ0,subQ5,subQ10,subQ11])],"isStart":true})});}
            var sketch = newSketch(context, id + "F16", { "sketchPlane" : qUnion([Q0])});
            skLineSegment(sketch, "E79", {"start": v(0, 74.25) * mm, "end": v(0, 104.25) * mm, "construction": true});
            skCircle(sketch, "E80", {"center": v(0, 104.25) * mm, "radius": 6 * mm});
            skArc(sketch, "E81", {"start": v(15, 104.25) * mm, "mid": v(0, 119.25) * mm, "end": v(-15, 104.25) * mm});
            skLineSegment(sketch, "E82", {"start": v(-15, 104.25) * mm, "end": v(-15, 92.25) * mm});
            skLineSegment(sketch, "E83", {"start": v(15, 104.25) * mm, "end": v(15, 92.25) * mm});
            skLineSegment(sketch, "E84", {"start": v(-15, 92.25) * mm, "end": v(-33, 74.25) * mm});
            skLineSegment(sketch, "E85", {"start": v(15, 92.25) * mm, "end": v(33, 74.25) * mm});
            skLineSegment(sketch, "E86", {"start": v(0, 0) * mm, "end": v(60, 0) * mm});
            skLineSegment(sketch, "E87.MirrorCS", {"start": v(15, -92.25) * mm, "end": v(33, -74.25) * mm});
            skLineSegment(sketch, "E88.MirrorCS", {"start": v(-15, -92.25) * mm, "end": v(-33, -74.25) * mm});
            skLineSegment(sketch, "E89.MirrorCS", {"start": v(0, -74.25) * mm, "end": v(0, -104.25) * mm, "construction": true});
            skLineSegment(sketch, "E90.MirrorCS", {"start": v(-15, -104.25) * mm, "end": v(-15, -92.25) * mm});
            skCircle(sketch, "E91.MirrorC", {"center": v(0, -104.25) * mm, "radius": 6 * mm});
            skArc(sketch, "E92.MirrorCS", {"start": v(15, -104.25) * mm, "mid": v(0, -119.25) * mm, "end": v(-15, -104.25) * mm});
            skLineSegment(sketch, "E93.MirrorCS", {"start": v(15, -104.25) * mm, "end": v(15, -92.25) * mm});
            skSolve(sketch);
        }
        {
            var Q0;
            Q0 = qSketchRegion(id + "F16", true);
            extrude(context, id + "F17", {"entities" : qUnion([Q0]), "operationType" : NewBodyOperationType.ADD, "depth" : 25 * mm, "offsetDistance" : 25 * mm});
        }
    });
